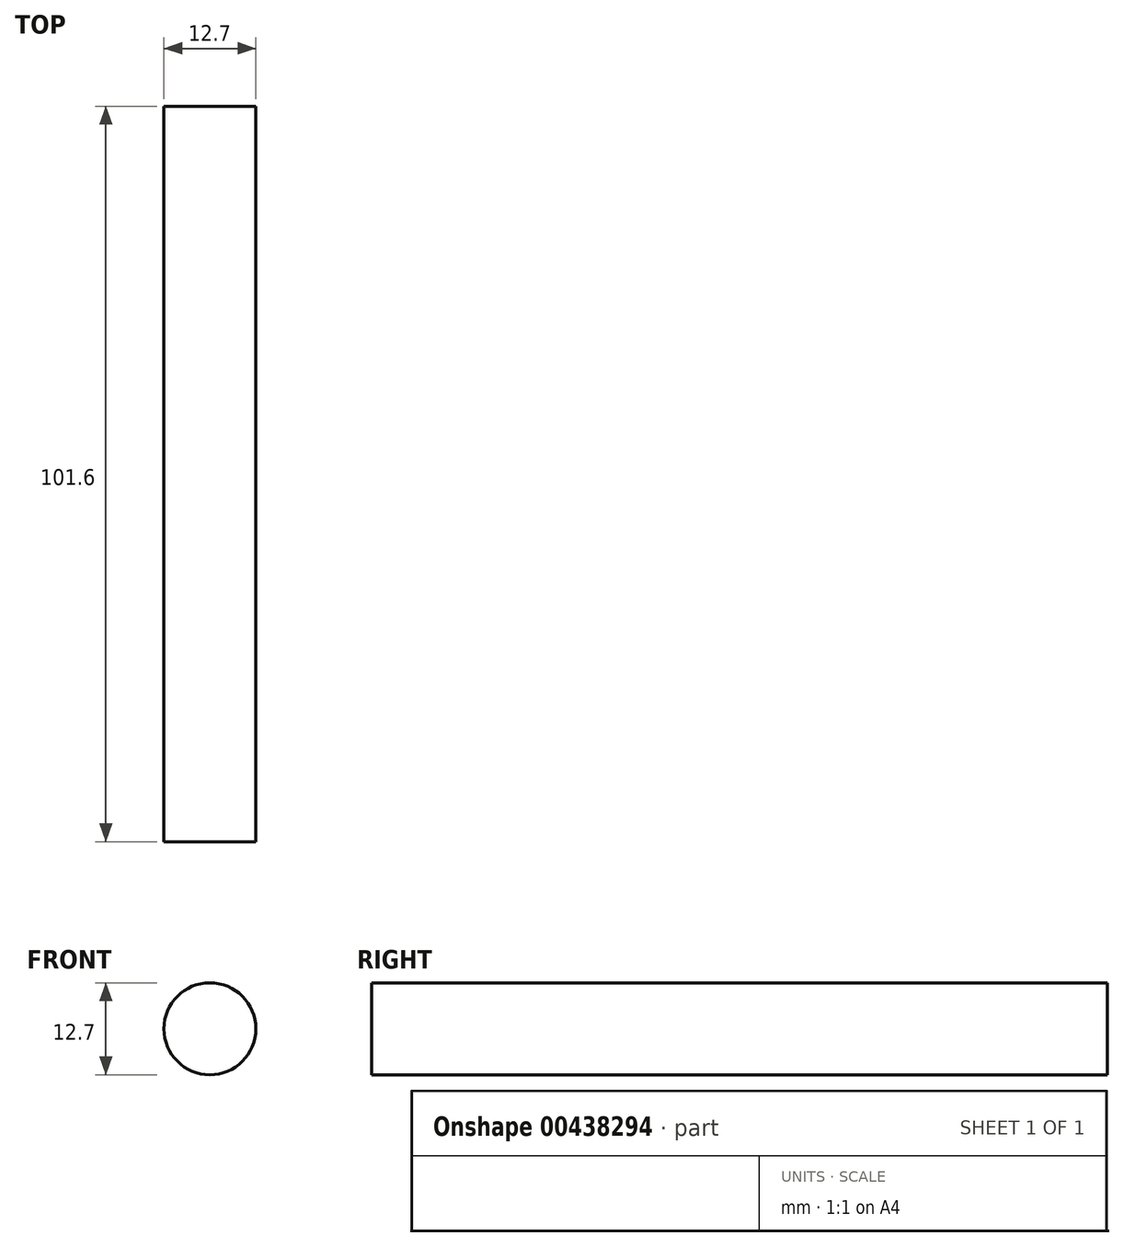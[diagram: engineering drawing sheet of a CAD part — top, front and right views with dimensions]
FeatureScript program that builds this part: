
annotation { "Feature Type Name" : "Feature", "Feature Type Description" : "" }
export const myFeature = defineFeature(function(context is Context, id is Id, definition is map)
    precondition{}
    {
        {
            var Q0;
            Q0=qCreatedBy(makeId("Front.planeOp"),FACE);
            var sketch = newSketch(context, id + "F0", { "sketchPlane" : qUnion([Q0])});
            skCircle(sketch, "E0", {"center": v(0, 0) * mm, "radius": 6.35 * mm});
            skSolve(sketch);
        }
        {
            var Q0;
            Q0=makeQuery(id+"F0.imprint","IMPRINT",FACE,{"disambiguationData":[TD([[makeQuery(id+"F0.imprint","IMPRINT",EDGE,{"derivedFrom":sQuery(id+"F0.wireOp",EDGE,"E0")}),1.0]])]});
            var Q1;
            Q1=sQuery(id+"F0.wireOp",EDGE,"E0");
            extrude(context, id + "F1", {"entities" : qUnion([Q0]), "surfaceEntities" : qUnion([Q1]), "depth" : 101.6 * mm});
        }
    });
